# Revit family: Haworth_MSeries_Storage_Caddy_AP_PRELIMINARY
name_source: partatom
category: Furniture Systems
units: mm (PartAtom-declared; Revit-internal decimal feet)

## family parameters
Always vertical = Yes
Cut with Voids When Loaded = No
OmniClass Number = 23.40.70.14.64.21
OmniClass Title = Systems Furniture
Part Type = Normal
Room Calculation Point = No
Round Connector Dimension = Use Diameter
Shared = No
Work Plane-Based = No

## types (4) — shared parameters
Actual Depth = 450 mm  [stored 1.47638 ft]
Assembly Code = E2020200
Bottom Case Offset = 30 mm  [stored 0.0984252 ft]
Bottom Drawer Height = 255 mm  [stored 0.836614 ft]
Box = Yes
Box File = Yes
Case Thickness = 20 mm  [stored 0.0656168 ft]
Caster Finish = Haworth _ Polymer _ Black
Description = Haworth - M Series - Storage - Caddy
Distance Between Drawer = 2 mm  [stored 0.00656168 ft]
Drawer Width = 409 mm  [stored 1.34186 ft]
File = Yes
Lock Finish = Haworth _ Polymer _ Black
Lock Offset Side = 50 mm  [stored 0.164042 ft]
Lock Offset Top = 30 mm  [stored 0.0984252 ft]
Manufacturer = Haworth
Max. Width = 1000 mm  [stored 3.28084 ft]
Middle Drawer Height = 180 mm  [stored 0.590551 ft]
Min. Width = 900 mm  [stored 2.95276 ft]
Model = STMSCMXX
One Drawer = Yes
Pencil Box File = No
Revision Number = 1
Size = Verify Final Dim. w/ Haworth
Top Drawer Height = 118 mm
Trim Finish = Haworth _ Polymer _ Black
Two Drawer = No
URL = https://www.haworth.com
URL - Product = https://www.haworth.com
Warranty = http://www.haworth.com

## per-type parameters (varying)
| type | Actual Height | Actual Width | Open Shelf | Open with Box File | Open with Pencil Box File | Pencil | Tambour Door | Tambour Door Height | Tambour Width | Tambour with Box File | Tambour with Pencil Box File | Total Drawer Height | Width |
| B/F 534h tambour | 534 mm  [stored 1.75197 ft] | 1000 mm  [stored 3.28084 ft] | No | No | No | No | Yes | 424 mm  [stored 1.39108 ft] | 573 mm  [stored 1.87992 ft] | Yes | No | 484 mm  [stored 1.58793 ft] | 1000 mm  [stored 3.28084 ft] |
| P/B/F 654h tambour | 654 mm  [stored 2.14567 ft] | 1000 mm  [stored 3.28084 ft] | No | No | No | Yes | Yes | 544 mm | 573 mm  [stored 1.87992 ft] | No | Yes | 604 mm  [stored 1.98163 ft] | 1000 mm  [stored 3.28084 ft] |
| B/F 534h open | 534 mm  [stored 1.75197 ft] | 900 mm  [stored 2.95276 ft] | Yes | Yes | No | No | No | 424 mm  [stored 1.39108 ft] | 473 mm  [stored 1.55184 ft] | No | No | 484 mm  [stored 1.58793 ft] | 900 mm  [stored 2.95276 ft] |
| P/B/F 654h open | 654 mm  [stored 2.14567 ft] | 900 mm  [stored 2.95276 ft] | Yes | No | Yes | Yes | No | 544 mm | 473 mm  [stored 1.55184 ft] | No | No | 604 mm  [stored 1.98163 ft] | 900 mm  [stored 2.95276 ft] |

note: [stored X ft] marks values corroborated as IEEE doubles in the binary element streams (Revit-internal decimal feet)

## geometry (parser evidence)
native form markers: Sweep x32
no freeform markers — native parametric forms only
